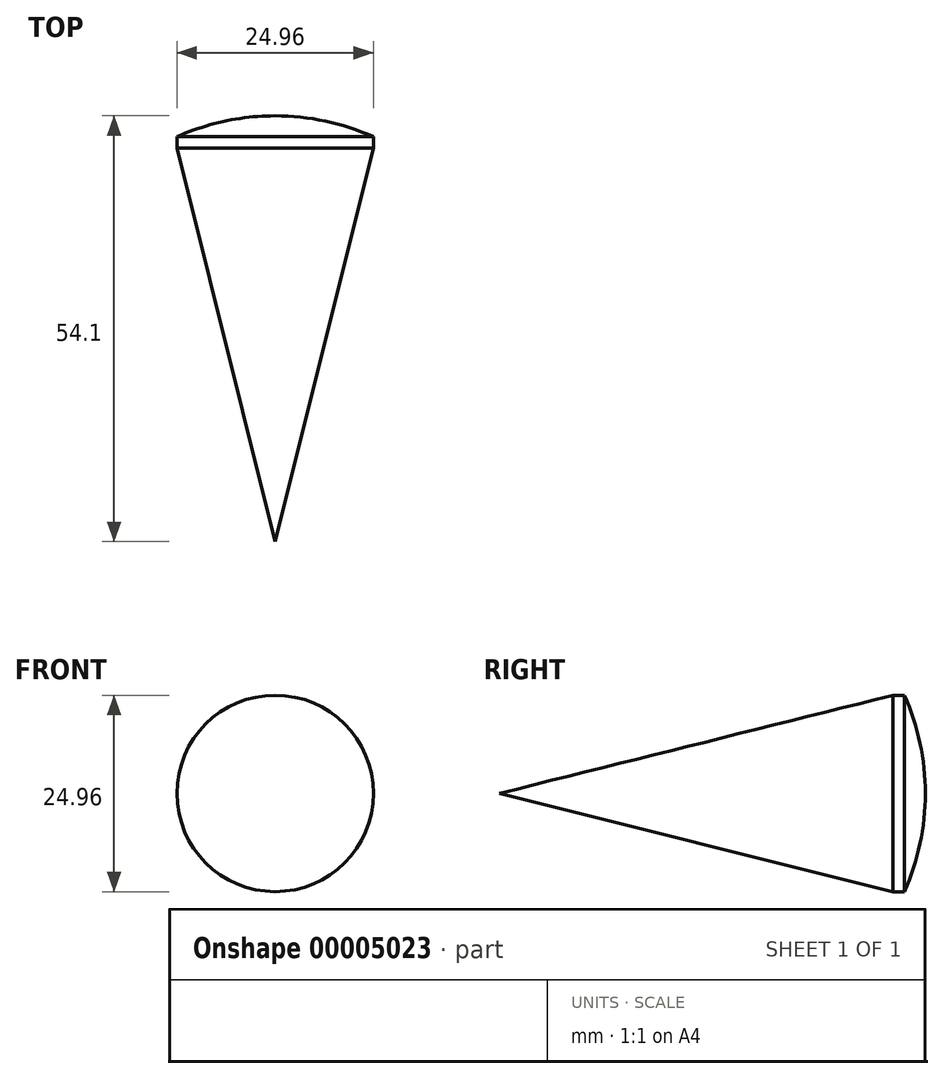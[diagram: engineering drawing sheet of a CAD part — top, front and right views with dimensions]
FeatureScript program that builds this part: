
annotation { "Feature Type Name" : "Feature", "Feature Type Description" : "" }
export const myFeature = defineFeature(function(context is Context, id is Id, definition is map)
    precondition{}
    {
        {
            var Q0;
            Q0=qCreatedBy(makeId("Top.planeOp"),FACE);
            var sketch = newSketch(context, id + "F0", { "sketchPlane" : qUnion([Q0])});
            skLineSegment(sketch, "E0", {"start": v(0, 0) * mm, "end": v(-12.47, 0) * mm});
            skLineSegment(sketch, "E1", {"start": v(-12.47, 0) * mm, "end": v(-12.47, 1.44) * mm});
            skLineSegment(sketch, "E2", {"start": v(0, 0) * mm, "end": v(0, 4.1) * mm});
            skArc(sketch, "E3", {"start": v(0, 4.1) * mm, "mid": v(-6.38, 3.43) * mm, "end": v(-12.47, 1.44) * mm});
            skLineSegment(sketch, "E4", {"start": v(0, 4.1) * mm, "end": v(3.22, 4.1) * mm, "construction": true});
            skSolve(sketch);
        }
        {
            var Q0;
            Q0=makeQuery(id+"F0.imprint","IMPRINT",FACE,{"disambiguationData":[TD([[makeQuery(id+"F0.imprint","IMPRINT",EDGE,{"derivedFrom":sQuery(id+"F0.wireOp",EDGE,"E0")}),-1.0]])]});
            var Q1;
            Q1=sQuery(id+"F0.wireOp",EDGE,"E2");
            revolve(context, id + "F1", {"entities" : qUnion([Q0]), "axis" : qUnion([Q1]), "revolveType" : RevolveType.FULL});
        }
        {
            var Q0;
            Q0=qCreatedBy(makeId("Top.planeOp"),FACE);
            var sketch = newSketch(context, id + "F2", { "sketchPlane" : qUnion([Q0])});
            skLineSegment(sketch, "E5.0", {"start": v(0, 0) * mm, "end": v(-12.47, 0) * mm});
            skLineSegment(sketch, "E6", {"start": v(-12.48, 0) * mm, "end": v(0, -50) * mm});
            skLineSegment(sketch, "E7", {"start": v(0, 0) * mm, "end": v(0, -50) * mm});
            skPoint(sketch, "E8.orphan", {"position": v(12.47, 0) * mm});
            skSolve(sketch);
        }
        {
            var Q0;
            Q0=makeQuery(id+"F2.imprint","IMPRINT",FACE,{"disambiguationData":[TD([[makeQuery(id+"F2.imprint","IMPRINT",EDGE,{"derivedFrom":sQuery(id+"F2.wireOp",EDGE,"E5.0")}),1.0]])]});
            var Q1;
            Q1=sQuery(id+"F2.wireOp",EDGE,"E7");
            revolve(context, id + "F3", {"entities" : qUnion([Q0]), "axis" : qUnion([Q1]), "revolveType" : RevolveType.FULL});
        }
    });
